# Revit family: Д_Eng
name_source: partatom
category: Mechanical Equipment
units: mm (PartAtom-declared; Revit-internal decimal feet)

## family parameters
Always vertical = Yes
Classification = None
Cut with Voids When Loaded = No
Part Type = Normal
Room Calculation Point = No
Round Connector Dimension = Use Diameter
Shared = No
Work Plane-Based = No

## types (3) — shared parameters
00_20_Manufacturer = Vents
00_20_Name = Axial fan
Amperage = 0 A
Casing Material = Plastic, opaque, white
Frequency = 50 Hz
L1 = 13 mm
Load Classification = HVAC
Maintenance zone material = <By Category>
Manufacturer = Vents
Number of Fase = 1
URL = https://ventilation-system.com
Voltage = 230 V
zero-valued in all types: Default Elevation

## per-type parameters (varying)
| type | B | D | Diameter | Dy | H | Height | L | L2 | Length | Maximum Air Flow | Panel | Power | Sound pressure level at 3 m distance | Weight | Width |
| 150 D | 212 mm  [stored 0.695538 ft] | 150 mm | 150 mm | 145 mm  [stored 0.475722 ft] | 212 mm  [stored 0.695538 ft] | 212 mm  [stored 0.695538 ft] | 132 mm  [stored 0.433071 ft] | 119 mm  [stored 0.39042 ft] | 132 mm  [stored 0.433071 ft] | 292.0 m³/h | Panel : 150 | 24 W | 38 dBA | 0.92 kg | 212 mm  [stored 0.695538 ft] |
| 100 D | 165 mm | 100 mm  [stored 0.328084 ft] | 100 mm  [stored 0.328084 ft] | 95 mm  [stored 0.31168 ft] | 165 mm | 165 mm | 109 mm | 96 mm  [stored 0.314961 ft] | 109 mm | 95.0 m³/h | Panel : 100 | 14 W | 34 dBA | 0.58 kg | 165 mm |
| 125 D | 190 mm | 125 mm  [stored 0.410105 ft] | 125 mm  [stored 0.410105 ft] | 120 mm  [stored 0.393701 ft] | 190 mm | 190 mm | 114 mm  [stored 0.374016 ft] | 102 mm | 114 mm  [stored 0.374016 ft] | 180.0 m³/h | Panel : 125 | 16 W | 35 dBA | 0.74 kg | 190 mm |

note: column(s) folded — value = type name in every type: 00_20_Type

note: [stored X ft] marks values corroborated as IEEE doubles in the binary element streams (Revit-internal decimal feet)
